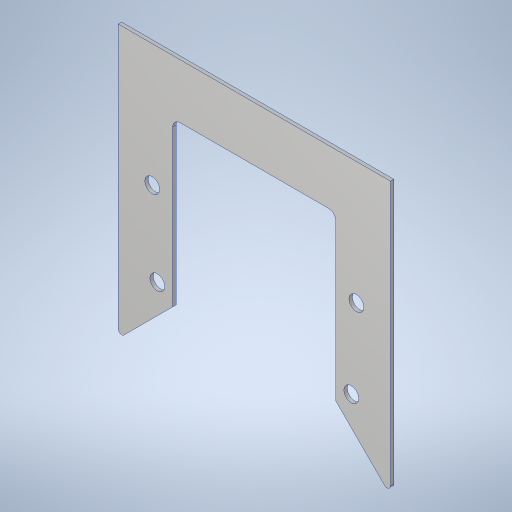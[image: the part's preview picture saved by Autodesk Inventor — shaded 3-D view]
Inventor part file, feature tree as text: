
AUTODESK INVENTOR PART (.ipt)
format: ipt  version: 2023.4 (Build 274418000, 418)  size: 265,728 bytes
history: native  units: in
note: dims shown in document units (in); Inventor stores cm internally (conversion verified against a paired STEP export)
features: fillet x2, sketch x2, extrude x1, hole x1
ambient origin geometry x8: Origin, YZ Plane, XZ Plane, XY Plane, X Axis, Y Axis, Z Axis, Center Point
bodies: Solid1 (feature_tree)
feature tree (6):
  extrude  "Extrusion1"  Depth=4.0in
  hole  "Hole1"  [1 undecoded]
  fillet  "Fillet1"  Radius=1.5in
  fillet  "Fillet2"  Radius=1.5in
  sketch  "Sketch1"  dims[d2=4.0in d3=4.0in]
  sketch  "Sketch2"  dims[d4=0.25in d5=0.0in d6=1.125in d7=1.5in d8=1.5in d9=1.125in d10=1.1in d11=0.75in d12=0.507in d13=0.25in d14=0.5635in d15=1.0in d16=0.8108in d18=6.004in d20=6.004in d21=4.0in d23=12.0in d25=5.0in d26=0.55in d27=0.25in]
note: 1 required parameter value undecoded (feature->parameter linkage not recoverable at this tier; creation-order binding heuristic only, values carry confidence <= 0.55)
